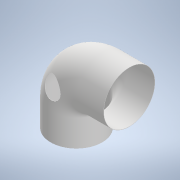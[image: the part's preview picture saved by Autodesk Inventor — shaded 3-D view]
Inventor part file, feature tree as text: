
AUTODESK INVENTOR PART (.ipt)
format: ipt  version: 2021 (Build 250183000, 183)  size: 196,608 bytes
history: native  units: mm
features: sketch x3, sweep x1, extrude x1
ambient origin geometry x8: Origin, YZ Plane, XZ Plane, XY Plane, X Axis, Y Axis, Z Axis, Center Point
bodies: Solid1 (feature_tree)
feature tree (5):
  sweep  "Sweep1"
  extrude  "Extrusion2"  Depth=20.0mm
  sketch  "Sketch1"  dims[d0=40.0mm d1=40.0mm]
  sketch  "Sketch2"  dims[d2=20.0mm d3=39.0mm]
  sketch  "Sketch4"  dims[d4=38.5mm d5=0.0mm d6=0.0mm d10=14.9mm d11=40.0mm d12=0.0mm d8=0.5mm d9=0.872665mm d13=0.5mm d14=0.872665mm]
